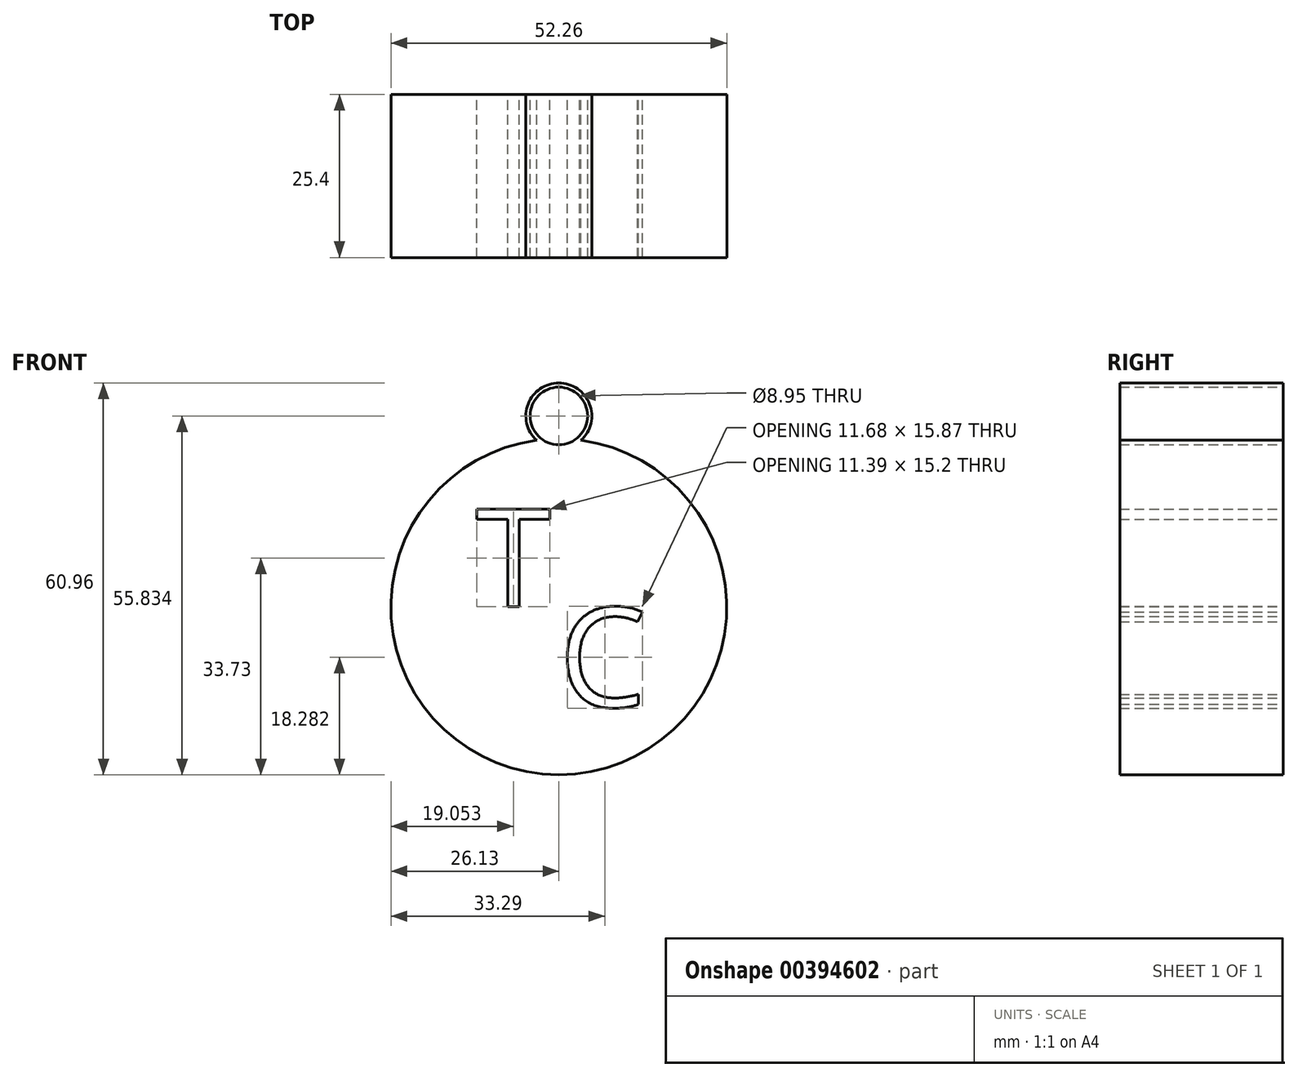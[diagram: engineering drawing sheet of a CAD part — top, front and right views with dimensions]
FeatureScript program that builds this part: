
annotation { "Feature Type Name" : "Feature", "Feature Type Description" : "" }
export const myFeature = defineFeature(function(context is Context, id is Id, definition is map)
    precondition{}
    {
        {
            var Q0;
            Q0=qCreatedBy(makeId("Front.planeOp"),FACE);
            var sketch = newSketch(context, id + "F0", { "sketchPlane" : qUnion([Q0])});
            skArc(sketch, "E0", {"start": v(-3.45, 25.9) * mm, "mid": v(0, -26.13) * mm, "end": v(3.45, 25.9) * mm});
            skText(sketch, "E1", { "text": "T", "fontName": "OpenSans-Regular.ttf"});
            skText(sketch, "E2", { "text": "C", "fontName": "OpenSans-Regular.ttf"});
            skCircle(sketch, "E3", {"center": v(0, 29.7) * mm, "radius": 5.13 * mm});
            skCircle(sketch, "E4", {"center": v(0, 29.7) * mm, "radius": 4.48 * mm});
            const initialGuessF0  = {"E1": [-0.01296, 0, 1, 0, 0.01533], "E2": [0, -0.01557, 1, 0, 0.01557]};
            skSetInitialGuess(sketch, initialGuessF0);
            skSolve(sketch);
        }
        {
            var Q0;
            {var subQ0=sQuery(id+"F0.wireOp",EDGE,"E0");Q0=makeQuery(id+"F0.imprint","IMPRINT",FACE,{"disambiguationData":[TD([[makeQuery(id+"F0.imprint","IMPRINT",EDGE,{"derivedFrom":subQ0}),1.0]])]});}
            var Q1;
            Q1=makeQuery(id+"F0.imprint","IMPRINT",FACE,{"disambiguationData":[TD([[makeQuery(id+"F0.imprint","IMPRINT",EDGE,{"derivedFrom":sQuery(id+"F0.wireOp",EDGE,"E4")}),-1.0]])]});
            extrude(context, id + "F1", {"entities" : qUnion([Q0, Q1]), "depth" : 25.4 * mm});
        }
    });
